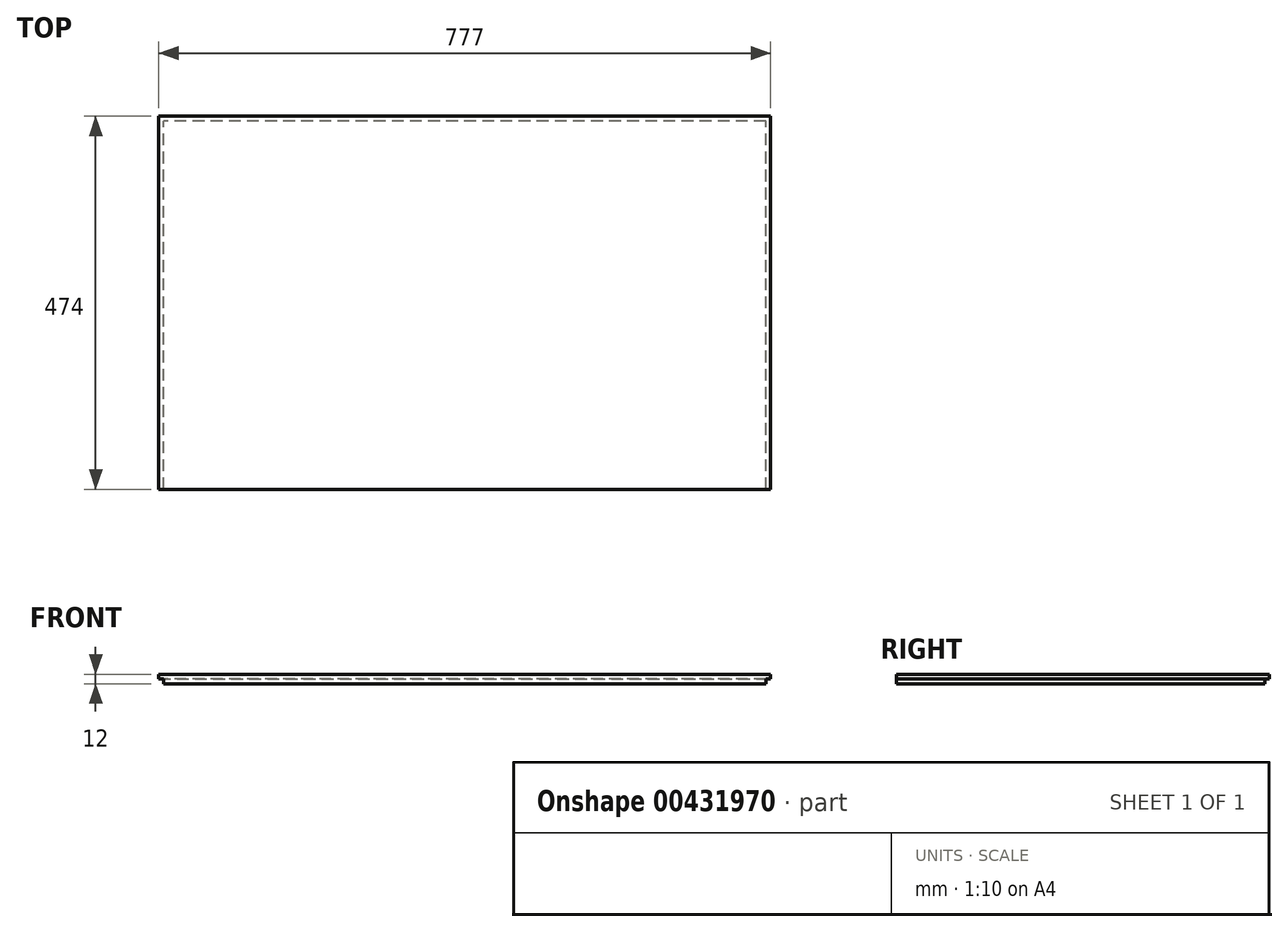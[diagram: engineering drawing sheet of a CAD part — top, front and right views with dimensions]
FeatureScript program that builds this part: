
annotation { "Feature Type Name" : "Feature", "Feature Type Description" : "" }
export const myFeature = defineFeature(function(context is Context, id is Id, definition is map)
    precondition{}
    {
        {
            var Q0;
            Q0=qCreatedBy(makeId("Top.planeOp"),FACE);
            var sketch = newSketch(context, id + "F0", { "sketchPlane" : qUnion([Q0])});
            skLineSegment(sketch, "E0.bottom", {"start": v(-388.5, 228.1) * mm, "end": v(388.5, 228.1) * mm});
            skLineSegment(sketch, "E0.top", {"start": v(-388.5, -245.9) * mm, "end": v(388.5, -245.9) * mm});
            skLineSegment(sketch, "E0.left", {"start": v(-388.5, 228.1) * mm, "end": v(-388.5, -245.9) * mm});
            skLineSegment(sketch, "E0.right", {"start": v(388.5, 228.1) * mm, "end": v(388.5, -245.9) * mm});
            skPoint(sketch, "E0.middle", {"position": v(0, -8.9) * mm});
            skSolve(sketch);
        }
        {
            var Q0;
            Q0=qSketchRegion(id+"F0",true);
            extrude(context, id + "F1", {"entities" : qUnion([Q0]), "depth" : 12 * mm, "offsetDistance" : 25 * mm});
        }
        {
            var Q0;
            Q0=makeQuery(id+"F1.opExtrude","CAP_FACE",FACE,{"disambiguationData":[OSD([sQuery(id+"F0.wireOp",EDGE,"E0.bottom"),sQuery(id+"F0.wireOp",EDGE,"E0.top"),sQuery(id+"F0.wireOp",EDGE,"E0.left"),sQuery(id+"F0.wireOp",EDGE,"E0.right")])],"isStart":true});
            var sketch = newSketch(context, id + "F2", { "sketchPlane" : qUnion([Q0])});
            skLineSegment(sketch, "E1.bottom", {"start": v(-388.5, 245.9) * mm, "end": v(-382.5, 245.9) * mm});
            skLineSegment(sketch, "E1.top", {"start": v(-388.5, -228.1) * mm, "end": v(-382.5, -228.1) * mm});
            skLineSegment(sketch, "E1.left", {"start": v(-388.5, 245.9) * mm, "end": v(-388.5, -228.1) * mm});
            skLineSegment(sketch, "E1.right", {"start": v(-382.5, 245.9) * mm, "end": v(-382.5, -228.1) * mm});
            skSolve(sketch);
        }
        {
            var Q0;
            Q0=qSketchRegion(id+"F2",true);
            extrude(context, id + "F3", {"entities" : qUnion([Q0]), "operationType" : NewBodyOperationType.REMOVE, "oppositeDirection" : true, "depth" : 6 * mm, "offsetDistance" : 25 * mm});
        }
        {
            var Q0;
            Q0=makeQuery(id+"F1.opExtrude","CAP_FACE",FACE,{"disambiguationData":[OSD([sQuery(id+"F0.wireOp",EDGE,"E0.bottom"),sQuery(id+"F0.wireOp",EDGE,"E0.top"),sQuery(id+"F0.wireOp",EDGE,"E0.left"),sQuery(id+"F0.wireOp",EDGE,"E0.right")])],"isStart":true});
            var sketch = newSketch(context, id + "F4", { "sketchPlane" : qUnion([Q0])});
            skLineSegment(sketch, "E2.bottom", {"start": v(388.5, 245.9) * mm, "end": v(382.5, 245.9) * mm});
            skLineSegment(sketch, "E2.top", {"start": v(388.5, -228.1) * mm, "end": v(382.5, -228.1) * mm});
            skLineSegment(sketch, "E2.left", {"start": v(388.5, 245.9) * mm, "end": v(388.5, -228.1) * mm});
            skLineSegment(sketch, "E2.right", {"start": v(382.5, 245.9) * mm, "end": v(382.5, -228.1) * mm});
            skSolve(sketch);
        }
        {
            var Q0;
            Q0=qSketchRegion(id+"F4",true);
            extrude(context, id + "F5", {"entities" : qUnion([Q0]), "operationType" : NewBodyOperationType.REMOVE, "oppositeDirection" : true, "depth" : 6 * mm, "offsetDistance" : 25 * mm});
        }
        {
            var Q0;
            Q0=makeQuery(id+"F1.opExtrude","CAP_FACE",FACE,{"disambiguationData":[OSD([sQuery(id+"F0.wireOp",EDGE,"E0.bottom"),sQuery(id+"F0.wireOp",EDGE,"E0.top"),sQuery(id+"F0.wireOp",EDGE,"E0.left"),sQuery(id+"F0.wireOp",EDGE,"E0.right")])],"isStart":true});
            var sketch = newSketch(context, id + "F6", { "sketchPlane" : qUnion([Q0])});
            skLineSegment(sketch, "E3.bottom", {"start": v(382.5, -228.1) * mm, "end": v(-382.5, -228.1) * mm});
            skLineSegment(sketch, "E3.top", {"start": v(382.5, -222.1) * mm, "end": v(-382.5, -222.1) * mm});
            skLineSegment(sketch, "E3.left", {"start": v(382.5, -228.1) * mm, "end": v(382.5, -222.1) * mm});
            skLineSegment(sketch, "E3.right", {"start": v(-382.5, -228.1) * mm, "end": v(-382.5, -222.1) * mm});
            skSolve(sketch);
        }
        {
            var Q0;
            Q0=qSketchRegion(id+"F6",true);
            extrude(context, id + "F7", {"entities" : qUnion([Q0]), "operationType" : NewBodyOperationType.REMOVE, "oppositeDirection" : true, "depth" : 6 * mm, "offsetDistance" : 25 * mm});
        }
    });
